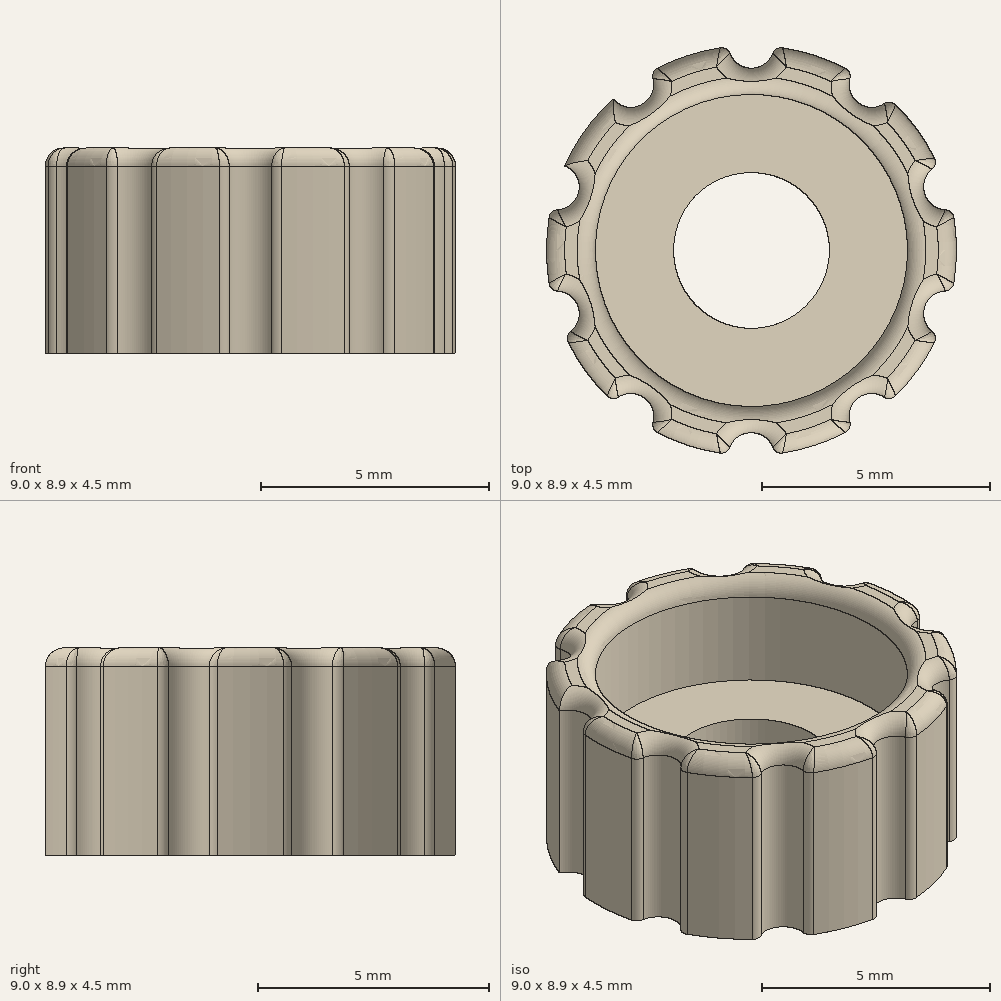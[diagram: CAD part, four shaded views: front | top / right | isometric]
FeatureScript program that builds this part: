
annotation { "Feature Type Name" : "Feature", "Feature Type Description" : "" }
export const myFeature = defineFeature(function(context is Context, id is Id, definition is map)
    precondition{}
    {
        {
            var Q0;
            Q0=qCreatedBy(makeId("Top.planeOp"),FACE);
            var sketch = newSketch(context, id + "F0", { "sketchPlane" : qUnion([Q0])});
            skCircle(sketch, "E0", {"center": v(0, 0) * mm, "radius": 3.43 * mm});
            skCircle(sketch, "E1", {"center": v(0, 0) * mm, "radius": 1.71 * mm});
            skCircle(sketch, "E2", {"center": v(0, 0) * mm, "radius": 4.5 * mm});
            skSolve(sketch);
        }
        {
            var Q0;
            Q0=makeQuery(id+"F0.imprint","IMPRINT",FACE,{"disambiguationData":[TD([[makeQuery(id+"F0.imprint","IMPRINT",EDGE,{"derivedFrom":sQuery(id+"F0.wireOp",EDGE,"E0")}),1.0]])]});
            extrude(context, id + "F1", {"entities" : qUnion([Q0]), "depth" : 2 * mm, "offsetDistance" : 25 * mm});
        }
        {
            var Q0;
            Q0=makeQuery(id+"F0.imprint","IMPRINT",FACE,{"disambiguationData":[TD([[makeQuery(id+"F0.imprint","IMPRINT",EDGE,{"derivedFrom":sQuery(id+"F0.wireOp",EDGE,"E0")}),-1.0]])]});
            extrude(context, id + "F2", {"entities" : qUnion([Q0]), "operationType" : NewBodyOperationType.ADD, "depth" : 4.5 * mm, "offsetDistance" : 25 * mm});
        }
        {
            var Q0;
            Q0=makeQuery(id+"F2.opExtrude","CAP_FACE",FACE,{"disambiguationData":[OSD([sQuery(id+"F0.wireOp",EDGE,"E0"),sQuery(id+"F0.wireOp",EDGE,"E2")])],"isStart":false});
            var sketch = newSketch(context, id + "F3", { "sketchPlane" : qUnion([Q0])});
            skCircle(sketch, "E3", {"center": v(0, 4.5) * mm, "radius": 0.5 * mm});
            skCircle(sketch, "E4.1.0", {"center": v(-2.65, 3.64) * mm, "radius": 0.5 * mm});
            skCircle(sketch, "E4.2.0", {"center": v(-4.28, 1.4) * mm, "radius": 0.5 * mm});
            skCircle(sketch, "E4.3.0", {"center": v(-4.28, -1.4) * mm, "radius": 0.5 * mm});
            skCircle(sketch, "E4.4.0", {"center": v(-2.65, -3.64) * mm, "radius": 0.5 * mm});
            skCircle(sketch, "E4.5.0", {"center": v(0, -4.5) * mm, "radius": 0.5 * mm});
            skCircle(sketch, "E4.6.0", {"center": v(2.65, -3.64) * mm, "radius": 0.5 * mm});
            skCircle(sketch, "E4.7.0", {"center": v(4.28, -1.4) * mm, "radius": 0.5 * mm});
            skCircle(sketch, "E4.8.0", {"center": v(4.28, 1.4) * mm, "radius": 0.5 * mm});
            skCircle(sketch, "E4.9.0", {"center": v(2.65, 3.64) * mm, "radius": 0.5 * mm});
            skPoint(sketch, "E4.center", {"position": v(0, 0) * mm});
            skSolve(sketch);
        }
        {
            var Q0;
            {var subQ0=sQuery(id+"F3.wireOp",EDGE,"E4.1.0");var subQ1=makeQuery(id+"F2.opExtrude","CAP_EDGE",EDGE,{"disambiguationData":[OSD([sQuery(id+"F0.wireOp",EDGE,"E2")])],"isStart":false});var subQ2=makeQuery(id+"F3.imprint","INTERSECT",VERTEX,{"disambiguationData":[OD(0.0)],"derivedFrom":[subQ1,subQ0]});Q0=makeQuery(id+"F3.imprint","IMPRINT",FACE,{"disambiguationData":[TD([[makeQuery(id+"F3.imprint","IMPRINT",EDGE,{"disambiguationData":[TD([[subQ2,-1.0]])],"derivedFrom":subQ0}),1.0]])]});}
            var Q1;
            {var subQ0=sQuery(id+"F3.wireOp",EDGE,"E3");var subQ1=makeQuery(id+"F2.opExtrude","CAP_EDGE",EDGE,{"disambiguationData":[OSD([sQuery(id+"F0.wireOp",EDGE,"E2")])],"isStart":false});var subQ2=makeQuery(id+"F3.imprint","INTERSECT",VERTEX,{"disambiguationData":[OD(0.0)],"derivedFrom":[subQ1,subQ0]});Q1=makeQuery(id+"F3.imprint","IMPRINT",FACE,{"disambiguationData":[TD([[makeQuery(id+"F3.imprint","IMPRINT",EDGE,{"disambiguationData":[TD([[subQ2,-1.0]])],"derivedFrom":subQ0}),1.0]])]});}
            var Q2;
            {var subQ0=sQuery(id+"F3.wireOp",EDGE,"E4.9.0");var subQ1=makeQuery(id+"F2.opExtrude","CAP_EDGE",EDGE,{"disambiguationData":[OSD([sQuery(id+"F0.wireOp",EDGE,"E2")])],"isStart":false});var subQ2=makeQuery(id+"F3.imprint","INTERSECT",VERTEX,{"disambiguationData":[OD(0.0)],"derivedFrom":[subQ1,subQ0]});Q2=makeQuery(id+"F3.imprint","IMPRINT",FACE,{"disambiguationData":[TD([[makeQuery(id+"F3.imprint","IMPRINT",EDGE,{"disambiguationData":[TD([[subQ2,-1.0]])],"derivedFrom":subQ0}),1.0]])]});}
            var Q3;
            {var subQ0=sQuery(id+"F3.wireOp",EDGE,"E4.8.0");var subQ1=makeQuery(id+"F2.opExtrude","CAP_EDGE",EDGE,{"disambiguationData":[OSD([sQuery(id+"F0.wireOp",EDGE,"E2")])],"isStart":false});var subQ2=makeQuery(id+"F3.imprint","INTERSECT",VERTEX,{"disambiguationData":[OD(0.0)],"derivedFrom":[subQ1,subQ0]});Q3=makeQuery(id+"F3.imprint","IMPRINT",FACE,{"disambiguationData":[TD([[makeQuery(id+"F3.imprint","IMPRINT",EDGE,{"disambiguationData":[TD([[subQ2,1.0]])],"derivedFrom":subQ0}),1.0]])]});}
            var Q4;
            {var subQ0=sQuery(id+"F3.wireOp",EDGE,"E4.7.0");var subQ1=makeQuery(id+"F2.opExtrude","CAP_EDGE",EDGE,{"disambiguationData":[OSD([sQuery(id+"F0.wireOp",EDGE,"E2")])],"isStart":false});var subQ2=makeQuery(id+"F3.imprint","INTERSECT",VERTEX,{"disambiguationData":[OD(0.0)],"derivedFrom":[subQ1,subQ0]});Q4=makeQuery(id+"F3.imprint","IMPRINT",FACE,{"disambiguationData":[TD([[makeQuery(id+"F3.imprint","IMPRINT",EDGE,{"disambiguationData":[TD([[subQ2,1.0]])],"derivedFrom":subQ0}),1.0]])]});}
            var Q5;
            {var subQ0=sQuery(id+"F3.wireOp",EDGE,"E4.6.0");var subQ1=makeQuery(id+"F2.opExtrude","CAP_EDGE",EDGE,{"disambiguationData":[OSD([sQuery(id+"F0.wireOp",EDGE,"E2")])],"isStart":false});var subQ2=makeQuery(id+"F3.imprint","INTERSECT",VERTEX,{"disambiguationData":[OD(0.0)],"derivedFrom":[subQ1,subQ0]});Q5=makeQuery(id+"F3.imprint","IMPRINT",FACE,{"disambiguationData":[TD([[makeQuery(id+"F3.imprint","IMPRINT",EDGE,{"disambiguationData":[TD([[subQ2,1.0]])],"derivedFrom":subQ0}),1.0]])]});}
            var Q6;
            {var subQ0=sQuery(id+"F3.wireOp",EDGE,"E4.5.0");var subQ1=makeQuery(id+"F2.opExtrude","CAP_EDGE",EDGE,{"disambiguationData":[OSD([sQuery(id+"F0.wireOp",EDGE,"E2")])],"isStart":false});var subQ2=makeQuery(id+"F3.imprint","INTERSECT",VERTEX,{"disambiguationData":[OD(0.0)],"derivedFrom":[subQ1,subQ0]});Q6=makeQuery(id+"F3.imprint","IMPRINT",FACE,{"disambiguationData":[TD([[makeQuery(id+"F3.imprint","IMPRINT",EDGE,{"disambiguationData":[TD([[subQ2,1.0]])],"derivedFrom":subQ0}),1.0]])]});}
            var Q7;
            {var subQ0=sQuery(id+"F3.wireOp",EDGE,"E4.4.0");var subQ1=makeQuery(id+"F2.opExtrude","CAP_EDGE",EDGE,{"disambiguationData":[OSD([sQuery(id+"F0.wireOp",EDGE,"E2")])],"isStart":false});var subQ2=makeQuery(id+"F3.imprint","INTERSECT",VERTEX,{"disambiguationData":[OD(0.0)],"derivedFrom":[subQ1,subQ0]});Q7=makeQuery(id+"F3.imprint","IMPRINT",FACE,{"disambiguationData":[TD([[makeQuery(id+"F3.imprint","IMPRINT",EDGE,{"disambiguationData":[TD([[subQ2,1.0]])],"derivedFrom":subQ0}),1.0]])]});}
            var Q8;
            {var subQ0=sQuery(id+"F3.wireOp",EDGE,"E4.3.0");var subQ1=makeQuery(id+"F2.opExtrude","CAP_EDGE",EDGE,{"disambiguationData":[OSD([sQuery(id+"F0.wireOp",EDGE,"E2")])],"isStart":false});var subQ2=makeQuery(id+"F3.imprint","INTERSECT",VERTEX,{"disambiguationData":[OD(0.0)],"derivedFrom":[subQ1,subQ0]});Q8=makeQuery(id+"F3.imprint","IMPRINT",FACE,{"disambiguationData":[TD([[makeQuery(id+"F3.imprint","IMPRINT",EDGE,{"disambiguationData":[TD([[subQ2,-1.0]])],"derivedFrom":subQ0}),1.0]])]});}
            var Q9;
            {var subQ0=sQuery(id+"F3.wireOp",EDGE,"E4.2.0");var subQ1=makeQuery(id+"F2.opExtrude","CAP_EDGE",EDGE,{"disambiguationData":[OSD([sQuery(id+"F0.wireOp",EDGE,"E2")])],"isStart":false});var subQ2=makeQuery(id+"F3.imprint","INTERSECT",VERTEX,{"disambiguationData":[OD(0.0)],"derivedFrom":[subQ1,subQ0]});Q9=makeQuery(id+"F3.imprint","IMPRINT",FACE,{"disambiguationData":[TD([[makeQuery(id+"F3.imprint","IMPRINT",EDGE,{"disambiguationData":[TD([[subQ2,-1.0]])],"derivedFrom":subQ0}),1.0]])]});}
            var Q10;
            {var subQ0=sQuery(id+"F0.wireOp",EDGE,"E0");Q10=makeQuery(id+"F2.boolean.opBoolean","MERGE",FACE,{"derivedFrom":[makeQuery(id+"F1.opExtrude","CAP_FACE",FACE,{"disambiguationData":[OSD([subQ0,sQuery(id+"F0.wireOp",EDGE,"E1")])],"isStart":true}),makeQuery(id+"F2.opExtrude","CAP_FACE",FACE,{"disambiguationData":[OSD([subQ0,sQuery(id+"F0.wireOp",EDGE,"E2")])],"isStart":true})]});}
            extrude(context, id + "F4", {"entities" : qUnion([Q0, Q1, Q2, Q3, Q4, Q5, Q6, Q7, Q8, Q9]), "operationType" : NewBodyOperationType.REMOVE, "endBound" : BoundingType.UP_TO_SURFACE, "oppositeDirection" : true, "depth" : 25 * mm, "endBoundEntityFace" : qUnion([Q10]), "offsetDistance" : 25 * mm});
        }
        {
            var Q0;
            {var subQ0=sQuery(id+"F3.wireOp",EDGE,"E3");var subQ1=sQuery(id+"F0.wireOp",EDGE,"E2");Q0=makeQuery(id+"F4.boolean.opBoolean","COPY",EDGE,{"derivedFrom":makeQuery(id+"F4.opExtrude","SWEPT_EDGE",EDGE,{"disambiguationData":[OSD([subQ1,subQ0]),TDD([makeQuery(id+"F3.imprint","INTERSECT",VERTEX,{"disambiguationData":[OD(1.0)],"derivedFrom":[makeQuery(id+"F2.opExtrude","CAP_EDGE",EDGE,{"disambiguationData":[OSD([subQ1])],"isStart":false}),subQ0]})])]})});}
            var Q1;
            {var subQ0=sQuery(id+"F3.wireOp",EDGE,"E3");var subQ1=sQuery(id+"F0.wireOp",EDGE,"E2");Q1=makeQuery(id+"F4.boolean.opBoolean","COPY",EDGE,{"derivedFrom":makeQuery(id+"F4.opExtrude","SWEPT_EDGE",EDGE,{"disambiguationData":[OSD([subQ1,subQ0]),TDD([makeQuery(id+"F3.imprint","INTERSECT",VERTEX,{"disambiguationData":[OD(0.0)],"derivedFrom":[makeQuery(id+"F2.opExtrude","CAP_EDGE",EDGE,{"disambiguationData":[OSD([subQ1])],"isStart":false}),subQ0]})])]})});}
            var Q2;
            {var subQ0=sQuery(id+"F3.wireOp",EDGE,"E4.9.0");var subQ1=sQuery(id+"F0.wireOp",EDGE,"E2");Q2=makeQuery(id+"F4.boolean.opBoolean","COPY",EDGE,{"derivedFrom":makeQuery(id+"F4.opExtrude","SWEPT_EDGE",EDGE,{"disambiguationData":[OSD([subQ1,subQ0]),TDD([makeQuery(id+"F3.imprint","INTERSECT",VERTEX,{"disambiguationData":[OD(0.0)],"derivedFrom":[makeQuery(id+"F2.opExtrude","CAP_EDGE",EDGE,{"disambiguationData":[OSD([subQ1])],"isStart":false}),subQ0]})])]})});}
            var Q3;
            {var subQ0=sQuery(id+"F3.wireOp",EDGE,"E4.9.0");var subQ1=sQuery(id+"F0.wireOp",EDGE,"E2");Q3=makeQuery(id+"F4.boolean.opBoolean","COPY",EDGE,{"derivedFrom":makeQuery(id+"F4.opExtrude","SWEPT_EDGE",EDGE,{"disambiguationData":[OSD([subQ1,subQ0]),TDD([makeQuery(id+"F3.imprint","INTERSECT",VERTEX,{"disambiguationData":[OD(1.0)],"derivedFrom":[makeQuery(id+"F2.opExtrude","CAP_EDGE",EDGE,{"disambiguationData":[OSD([subQ1])],"isStart":false}),subQ0]})])]})});}
            var Q4;
            {var subQ0=sQuery(id+"F3.wireOp",EDGE,"E4.8.0");var subQ1=sQuery(id+"F0.wireOp",EDGE,"E2");Q4=makeQuery(id+"F4.boolean.opBoolean","COPY",EDGE,{"derivedFrom":makeQuery(id+"F4.opExtrude","SWEPT_EDGE",EDGE,{"disambiguationData":[OSD([subQ1,subQ0]),TDD([makeQuery(id+"F3.imprint","INTERSECT",VERTEX,{"disambiguationData":[OD(1.0)],"derivedFrom":[makeQuery(id+"F2.opExtrude","CAP_EDGE",EDGE,{"disambiguationData":[OSD([subQ1])],"isStart":false}),subQ0]})])]})});}
            var Q5;
            {var subQ0=sQuery(id+"F3.wireOp",EDGE,"E4.8.0");var subQ1=sQuery(id+"F0.wireOp",EDGE,"E2");Q5=makeQuery(id+"F4.boolean.opBoolean","COPY",EDGE,{"derivedFrom":makeQuery(id+"F4.opExtrude","SWEPT_EDGE",EDGE,{"disambiguationData":[OSD([subQ1,subQ0]),TDD([makeQuery(id+"F3.imprint","INTERSECT",VERTEX,{"disambiguationData":[OD(0.0)],"derivedFrom":[makeQuery(id+"F2.opExtrude","CAP_EDGE",EDGE,{"disambiguationData":[OSD([subQ1])],"isStart":false}),subQ0]})])]})});}
            var Q6;
            {var subQ0=sQuery(id+"F3.wireOp",EDGE,"E4.7.0");var subQ1=sQuery(id+"F0.wireOp",EDGE,"E2");Q6=makeQuery(id+"F4.boolean.opBoolean","COPY",EDGE,{"derivedFrom":makeQuery(id+"F4.opExtrude","SWEPT_EDGE",EDGE,{"disambiguationData":[OSD([subQ1,subQ0]),TDD([makeQuery(id+"F3.imprint","INTERSECT",VERTEX,{"disambiguationData":[OD(1.0)],"derivedFrom":[makeQuery(id+"F2.opExtrude","CAP_EDGE",EDGE,{"disambiguationData":[OSD([subQ1])],"isStart":false}),subQ0]})])]})});}
            var Q7;
            {var subQ0=sQuery(id+"F3.wireOp",EDGE,"E4.7.0");var subQ1=sQuery(id+"F0.wireOp",EDGE,"E2");Q7=makeQuery(id+"F4.boolean.opBoolean","COPY",EDGE,{"derivedFrom":makeQuery(id+"F4.opExtrude","SWEPT_EDGE",EDGE,{"disambiguationData":[OSD([subQ1,subQ0]),TDD([makeQuery(id+"F3.imprint","INTERSECT",VERTEX,{"disambiguationData":[OD(0.0)],"derivedFrom":[makeQuery(id+"F2.opExtrude","CAP_EDGE",EDGE,{"disambiguationData":[OSD([subQ1])],"isStart":false}),subQ0]})])]})});}
            var Q8;
            {var subQ0=sQuery(id+"F3.wireOp",EDGE,"E4.6.0");var subQ1=sQuery(id+"F0.wireOp",EDGE,"E2");Q8=makeQuery(id+"F4.boolean.opBoolean","COPY",EDGE,{"derivedFrom":makeQuery(id+"F4.opExtrude","SWEPT_EDGE",EDGE,{"disambiguationData":[OSD([subQ1,subQ0]),TDD([makeQuery(id+"F3.imprint","INTERSECT",VERTEX,{"disambiguationData":[OD(1.0)],"derivedFrom":[makeQuery(id+"F2.opExtrude","CAP_EDGE",EDGE,{"disambiguationData":[OSD([subQ1])],"isStart":false}),subQ0]})])]})});}
            var Q9;
            {var subQ0=sQuery(id+"F3.wireOp",EDGE,"E4.6.0");var subQ1=sQuery(id+"F0.wireOp",EDGE,"E2");Q9=makeQuery(id+"F4.boolean.opBoolean","COPY",EDGE,{"derivedFrom":makeQuery(id+"F4.opExtrude","SWEPT_EDGE",EDGE,{"disambiguationData":[OSD([subQ1,subQ0]),TDD([makeQuery(id+"F3.imprint","INTERSECT",VERTEX,{"disambiguationData":[OD(0.0)],"derivedFrom":[makeQuery(id+"F2.opExtrude","CAP_EDGE",EDGE,{"disambiguationData":[OSD([subQ1])],"isStart":false}),subQ0]})])]})});}
            var Q10;
            {var subQ0=sQuery(id+"F3.wireOp",EDGE,"E4.5.0");var subQ1=sQuery(id+"F0.wireOp",EDGE,"E2");Q10=makeQuery(id+"F4.boolean.opBoolean","COPY",EDGE,{"derivedFrom":makeQuery(id+"F4.opExtrude","SWEPT_EDGE",EDGE,{"disambiguationData":[OSD([subQ1,subQ0]),TDD([makeQuery(id+"F3.imprint","INTERSECT",VERTEX,{"disambiguationData":[OD(1.0)],"derivedFrom":[makeQuery(id+"F2.opExtrude","CAP_EDGE",EDGE,{"disambiguationData":[OSD([subQ1])],"isStart":false}),subQ0]})])]})});}
            var Q11;
            {var subQ0=sQuery(id+"F3.wireOp",EDGE,"E4.5.0");var subQ1=sQuery(id+"F0.wireOp",EDGE,"E2");Q11=makeQuery(id+"F4.boolean.opBoolean","COPY",EDGE,{"derivedFrom":makeQuery(id+"F4.opExtrude","SWEPT_EDGE",EDGE,{"disambiguationData":[OSD([subQ1,subQ0]),TDD([makeQuery(id+"F3.imprint","INTERSECT",VERTEX,{"disambiguationData":[OD(0.0)],"derivedFrom":[makeQuery(id+"F2.opExtrude","CAP_EDGE",EDGE,{"disambiguationData":[OSD([subQ1])],"isStart":false}),subQ0]})])]})});}
            var Q12;
            {var subQ0=sQuery(id+"F3.wireOp",EDGE,"E4.4.0");var subQ1=sQuery(id+"F0.wireOp",EDGE,"E2");Q12=makeQuery(id+"F4.boolean.opBoolean","COPY",EDGE,{"derivedFrom":makeQuery(id+"F4.opExtrude","SWEPT_EDGE",EDGE,{"disambiguationData":[OSD([subQ1,subQ0]),TDD([makeQuery(id+"F3.imprint","INTERSECT",VERTEX,{"disambiguationData":[OD(1.0)],"derivedFrom":[makeQuery(id+"F2.opExtrude","CAP_EDGE",EDGE,{"disambiguationData":[OSD([subQ1])],"isStart":false}),subQ0]})])]})});}
            var Q13;
            {var subQ0=sQuery(id+"F3.wireOp",EDGE,"E4.4.0");var subQ1=sQuery(id+"F0.wireOp",EDGE,"E2");Q13=makeQuery(id+"F4.boolean.opBoolean","COPY",EDGE,{"derivedFrom":makeQuery(id+"F4.opExtrude","SWEPT_EDGE",EDGE,{"disambiguationData":[OSD([subQ1,subQ0]),TDD([makeQuery(id+"F3.imprint","INTERSECT",VERTEX,{"disambiguationData":[OD(0.0)],"derivedFrom":[makeQuery(id+"F2.opExtrude","CAP_EDGE",EDGE,{"disambiguationData":[OSD([subQ1])],"isStart":false}),subQ0]})])]})});}
            var Q14;
            {var subQ0=sQuery(id+"F3.wireOp",EDGE,"E4.3.0");var subQ1=sQuery(id+"F0.wireOp",EDGE,"E2");Q14=makeQuery(id+"F4.boolean.opBoolean","COPY",EDGE,{"derivedFrom":makeQuery(id+"F4.opExtrude","SWEPT_EDGE",EDGE,{"disambiguationData":[OSD([subQ1,subQ0]),TDD([makeQuery(id+"F3.imprint","INTERSECT",VERTEX,{"disambiguationData":[OD(0.0)],"derivedFrom":[makeQuery(id+"F2.opExtrude","CAP_EDGE",EDGE,{"disambiguationData":[OSD([subQ1])],"isStart":false}),subQ0]})])]})});}
            var Q15;
            {var subQ0=sQuery(id+"F3.wireOp",EDGE,"E4.3.0");var subQ1=sQuery(id+"F0.wireOp",EDGE,"E2");Q15=makeQuery(id+"F4.boolean.opBoolean","COPY",EDGE,{"derivedFrom":makeQuery(id+"F4.opExtrude","SWEPT_EDGE",EDGE,{"disambiguationData":[OSD([subQ1,subQ0]),TDD([makeQuery(id+"F3.imprint","INTERSECT",VERTEX,{"disambiguationData":[OD(1.0)],"derivedFrom":[makeQuery(id+"F2.opExtrude","CAP_EDGE",EDGE,{"disambiguationData":[OSD([subQ1])],"isStart":false}),subQ0]})])]})});}
            var Q16;
            {var subQ0=sQuery(id+"F3.wireOp",EDGE,"E4.2.0");var subQ1=sQuery(id+"F0.wireOp",EDGE,"E2");Q16=makeQuery(id+"F4.boolean.opBoolean","COPY",EDGE,{"derivedFrom":makeQuery(id+"F4.opExtrude","SWEPT_EDGE",EDGE,{"disambiguationData":[OSD([subQ1,subQ0]),TDD([makeQuery(id+"F3.imprint","INTERSECT",VERTEX,{"disambiguationData":[OD(0.0)],"derivedFrom":[makeQuery(id+"F2.opExtrude","CAP_EDGE",EDGE,{"disambiguationData":[OSD([subQ1])],"isStart":false}),subQ0]})])]})});}
            var Q17;
            {var subQ0=sQuery(id+"F3.wireOp",EDGE,"E4.2.0");var subQ1=sQuery(id+"F0.wireOp",EDGE,"E2");Q17=makeQuery(id+"F4.boolean.opBoolean","COPY",EDGE,{"derivedFrom":makeQuery(id+"F4.opExtrude","SWEPT_EDGE",EDGE,{"disambiguationData":[OSD([subQ1,subQ0]),TDD([makeQuery(id+"F3.imprint","INTERSECT",VERTEX,{"disambiguationData":[OD(1.0)],"derivedFrom":[makeQuery(id+"F2.opExtrude","CAP_EDGE",EDGE,{"disambiguationData":[OSD([subQ1])],"isStart":false}),subQ0]})])]})});}
            var Q18;
            {var subQ0=sQuery(id+"F3.wireOp",EDGE,"E4.1.0");var subQ1=sQuery(id+"F0.wireOp",EDGE,"E2");Q18=makeQuery(id+"F4.boolean.opBoolean","COPY",EDGE,{"derivedFrom":makeQuery(id+"F4.opExtrude","SWEPT_EDGE",EDGE,{"disambiguationData":[OSD([subQ1,subQ0]),TDD([makeQuery(id+"F3.imprint","INTERSECT",VERTEX,{"disambiguationData":[OD(0.0)],"derivedFrom":[makeQuery(id+"F2.opExtrude","CAP_EDGE",EDGE,{"disambiguationData":[OSD([subQ1])],"isStart":false}),subQ0]})])]})});}
            var Q19;
            {var subQ0=sQuery(id+"F3.wireOp",EDGE,"E4.1.0");var subQ1=sQuery(id+"F0.wireOp",EDGE,"E2");Q19=makeQuery(id+"F4.boolean.opBoolean","COPY",EDGE,{"derivedFrom":makeQuery(id+"F4.opExtrude","SWEPT_EDGE",EDGE,{"disambiguationData":[OSD([subQ1,subQ0]),TDD([makeQuery(id+"F3.imprint","INTERSECT",VERTEX,{"disambiguationData":[OD(1.0)],"derivedFrom":[makeQuery(id+"F2.opExtrude","CAP_EDGE",EDGE,{"disambiguationData":[OSD([subQ1])],"isStart":false}),subQ0]})])]})});}
            fillet(context, id + "F5", {"entities" : qUnion([Q0, Q1, Q2, Q3, Q4, Q5, Q6, Q7, Q8, Q9, Q10, Q11, Q12, Q13, Q14, Q15, Q16, Q17, Q18, Q19]), "radius" : 0.2 * mm, "tangentPropagation" : true, "allowEdgeOverflow" : false});
        }
        {
            var Q0;
            Q0=makeQuery(id+"F2.opExtrude","CAP_FACE",FACE,{"disambiguationData":[OSD([sQuery(id+"F0.wireOp",EDGE,"E0"),sQuery(id+"F0.wireOp",EDGE,"E2")])],"isStart":false});
            fillet(context, id + "F6", {"entities" : qUnion([Q0]), "radius" : 0.4 * mm, "tangentPropagation" : true, "allowEdgeOverflow" : false});
        }
    });
